# Revit family: Sink-Kitchen-KOHLER-Vault-K-3821
name_source: partatom
category: Plumbing Fixtures
revit_build: Autodesk Revit 2015 (Build: 20140606_1530(x64)
units: mm (PartAtom-declared; Revit-internal decimal feet)

## types (3) — shared parameters
ADA Compliant = No
Assembly Code = D2010400
CW Connection = No
Cold Water Inlet = Cold Water Inlet
Date Modified = 08/02/2018
Default Elevation = 36"
Drain Included = No
Finish = Kohler-Metal-NA-Stainless
HW Connection = No
Height = 9 5/16"
Hot Water Inlet = Hot Water Inlet
Length = 33"
Manufacturer = KOHLER Co.
MasterFormat 1995 = 15410
MasterFormat 2004 = 22.41.16
Material = 18-Gauge Stainless Steel
Product Documentation Link = http://www.us.kohler.com
Product Name = Vault
Product Page URL = http://www.us.kohler.com
URL = https://www.us.kohler.com
Vent Connection = No
Waste Connection = Yes
Waste Water Outlet = Waste Water Outlet
Width = 22"

## per-type parameters (varying)
| type | 1_Hole | 3_Hole | 4_Hole | Description | Model | Type |
| 1 faucet hole, NA-Stainless Steel | Yes | No | No | 33inch x 22inch x 9-5/16inch top-/under-mount large single-bowl kitchen sink with single faucet hole | K-3821-1-NA | 1 |
| 3 faucet hole, NA-Stainless Steel | No | Yes | No | 33inch x 22inch x 9-5/16inch top-/under-mount large single-bowl kitchen sink with 3 faucet holes | K-3821-3-NA | 2 |
| 4 faucet hole, NA-Stainless Steel | No | No | Yes | 33inch x 22inch x 9-5/16inch top-/under-mount large single-bowl kitchen sink with 4 faucet holes | K-3821-4-NA | 3 |

## geometry (parser evidence)
native form markers: Sweep x4
no freeform markers — native parametric forms only
